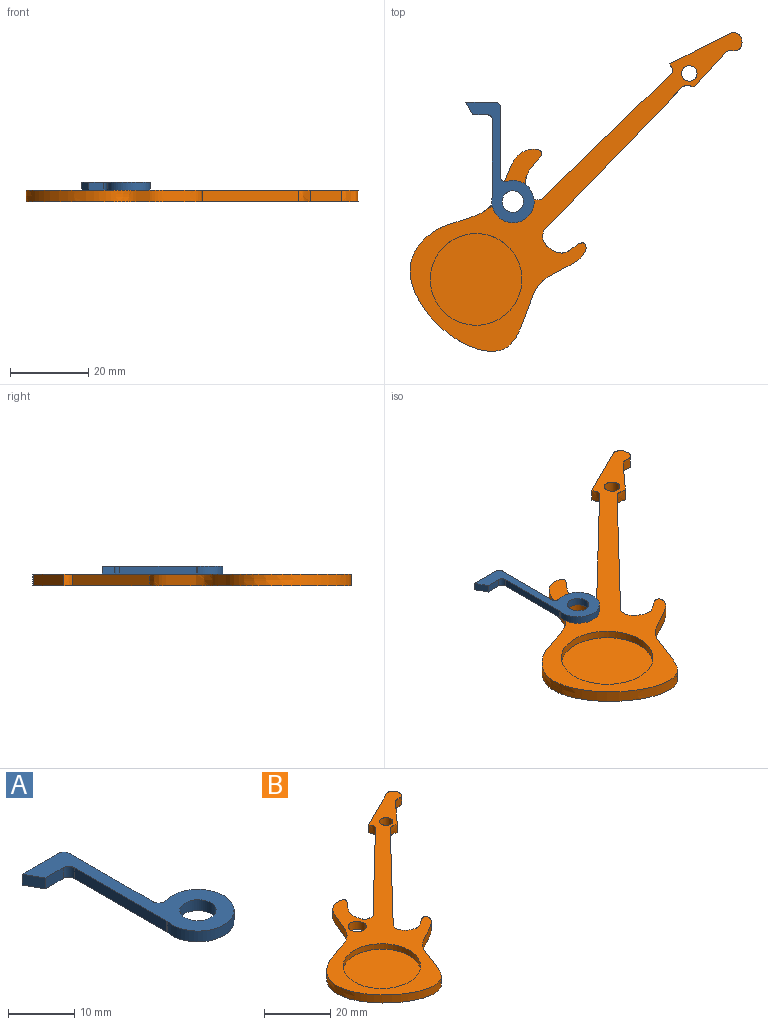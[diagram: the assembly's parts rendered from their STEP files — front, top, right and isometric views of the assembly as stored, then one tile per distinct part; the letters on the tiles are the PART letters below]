
ASSEMBLY  parts=2 mates=1
PART A: 13 faces, bbox 17.5x30.8x2 mm
  f0: plane 30.83x17.53mm, normal (0,0,1), area 135.1mm2, adj f2,f3,f4,f5,f6,f7,f8,f9
  f1: plane 30.83x17.53mm, normal (0,0,-1), area 135.1mm2, adj f2,f3,f4,f5,f6,f7,f8,f9
  f2: cylinder r=1.2mm len=2mm, axis (0,0,-1), area 4.5mm2, adj f0,f1,f3,f11
  f3: plane 17.86x2mm, normal (1,0,0), area 35.7mm2, adj f0,f1,f2,f4
  f4: cylinder r=1.2mm len=2mm, axis (0,0,-1), area 3.8mm2, adj f0,f1,f3,f5
  f5: plane 7.68x2mm, normal (0,1,0), area 15.4mm2, adj f0,f1,f4,f6
  f6: plane 3.19x2mm, normal (-0.87,-0.49,0), area 7.3mm2, adj f0,f1,f5,f7
  f7: plane 3.81x2mm, normal (0,-1,0), area 7.6mm2, adj f0,f1,f6,f8
  f8: cylinder r=1.2mm len=2mm, axis (0,0,-1), area 3.8mm2, adj f0,f1,f7,f9
  f9: plane 19.67x2mm, normal (-1,0,0), area 39.3mm2, adj f0,f1,f8,f10
  f10: cylinder r=1.2mm len=2mm, axis (0,0,-1), area 0.5mm2, adj f0,f1,f9,f11
  f11: cylinder r=5.44mm len=10.88mm, axis (0,0,-1), area 56.8mm2, adj f0,f1,f2,f10
  f12: cylinder r=2.75mm len=5.5mm, axis (0,0,-1), area 34.6mm2, adj f0,f1
PART B: 14 faces, bbox 85.5x82.1x3 mm
  f0: plane 8.86x8.01mm, normal (0.74,-0.67,0), area 35.8mm2, adj f1,f9,f10,f11
  f1: extruded ~5.04x4.16mm, area 31.2mm2, adj f0,f2,f10,f11
  f2: plane 15.32x7.68mm, normal (-0.45,0.89,0), area 51.4mm2, adj f1,f3,f10,f11
  f3: extruded ~3x2.33mm, area 7.5mm2, adj f2,f4,f10,f11
  f4: plane 33.43x32.37mm, normal (-0.7,0.72,0), area 139.6mm2, adj f3,f5,f10,f11
  f5: extruded ~51.44x44.88mm, area 451.4mm2, adj f4,f6,f10,f11
  f6: plane 36.79x35.5mm, normal (0.72,-0.69,0), area 153.4mm2, adj f5,f9,f10,f11
  f7: cylinder r=2mm len=4mm, axis (0,0,1), area 37.7mm2, adj f10,f11
  f8: cylinder r=2.75mm len=5.5mm, axis (0,0,1), area 51.8mm2, adj f10,f11
  f9: extruded ~3.04x3mm, area 9.5mm2, adj f0,f6,f10,f11
  f10: plane 85.46x82.09mm, normal (0,0,-1), area 1436.3mm2, adj f0,f1,f2,f3,f4,f5,f6,f7
  f11: plane 85.46x82.09mm, normal (0,0,1), area 1002.6mm2, adj f0,f1,f2,f3,f4,f5,f6,f7
  f12: cylinder r=11.75mm len=23.5mm, axis (0,0,1), area 147.7mm2, adj f11,f13
  f13: plane 23.5x23.5mm, normal (0,0,1), area 433.7mm2, adj f12
PLACE A t=(-8.63,-14.22,-5.59)mm
PLACE B t=(-12.46,16,-5.59)mm
MATE revolute B.f8 <-> A.f11  axis (0,0,1) through (-38.4,3.08,-5.59)mm
